# Revit family: Stex 45 MP-S
name_source: partatom
category: HLS-Bauteile
units: mm (PartAtom-declared; Revit-internal decimal feet)

## family parameters
Arbeitsebenenbasiert = Ja
Beim Laden mit Abzugskörper schneiden = Nein
Bemaßung runder Anschluss = Durchmesser verwenden
Beschriftungsausrichtung beibehalten = Nein
Gemeinsam genutzt = Ja
Immer vertikal = Nein
Klassifizierung = Keine
Raumberechnungspunkt = Nein
Teiletyp = Normal

## types (3) — shared parameters
Breite = 62 mm  [stored 0.203412 ft]
Fabrikat = MEFA
Form = einschwenkbar
Kurztext1 = Stex 45 Montageplatte MP-S
Länge = 38 mm  [stored 0.124672 ft]
Material = Stahl
Materialname = S235
Mengeneinheit = St
Profil = C-Profil
Profiltyp = 45
Vorgabe-Ansicht = 1219 mm
vpe = 50

## per-type parameters (varying)
| type | Artikelnummer | EAN | Gewicht | Gewicht pro Bauteil | Gewinde | Kurztext2 | Zahnplatte |
| Stex 45 MP-S M12 | 0818106 | 4250928466594 | 0,04 kg | 0,04 kg | M12 | M12 ZnNi | Zahnplatte S : Zahnplatte S M12 |
| Stex 45 MP-S M10 | 0818105 | 4250928466587 | 0,04 kg | 0,04 kg | M10 | M10 ZnNi | Zahnplatte S : Zahnplatte S M10 |
| Stex 45 MP-S M8 | 0818104 | 4250928466570 | 0,05 kg | 0,05 kg | M8 | M8 ZnNi | Zahnplatte S : Zahnplatte S M 8 |

note: [stored X ft] marks values corroborated as IEEE doubles in the binary element streams (Revit-internal decimal feet)
